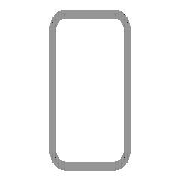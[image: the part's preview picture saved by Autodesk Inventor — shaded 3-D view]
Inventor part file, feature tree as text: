
AUTODESK INVENTOR PART (.ipt)
format: ipt  version: 2025 (Build 290162010, 162A)  size: 156,160 bytes
history: native  units: mm (DEFAULTED — no unit token found)
features: other x3, sketch x2, projected_geometry x2, extrude x1, plane x1
ambient origin geometry x8: Origin, YZ Plane, XZ Plane, XY Plane, X Axis, Y Axis, Z Axis, Center Point
bodies: Solid1 (feature_tree), Body (feature_tree)
feature tree (9):
  other  "Driven Length"
  other  "Start plane"
  other  "End plane"
  extrude  "Extrusion2"  TaperAngle=0.0deg  [1 undecoded]
  sketch  "Sketch3"  dims[d3=1800.0mm d4=0.0mm]
  plane  "Work Plane3"
  sketch  "Sketch5"  dims[d7=4.0mm d9=20.0mm d11=40.0mm d12=2.0mm d13=-0.0mm d14=1800.0mm d15=10.0mm d16=20.0mm d17=90.0deg d18=1800.0mm d19=9.599311mm d20=6.108652mm d21=0.0mm d22=0.0mm]
  projected_geometry  "Projected Loop1"
  projected_geometry  "Projected Loop2"
note: 1 required parameter value undecoded (feature->parameter linkage not recoverable at this tier; creation-order binding heuristic only, values carry confidence <= 0.55)
